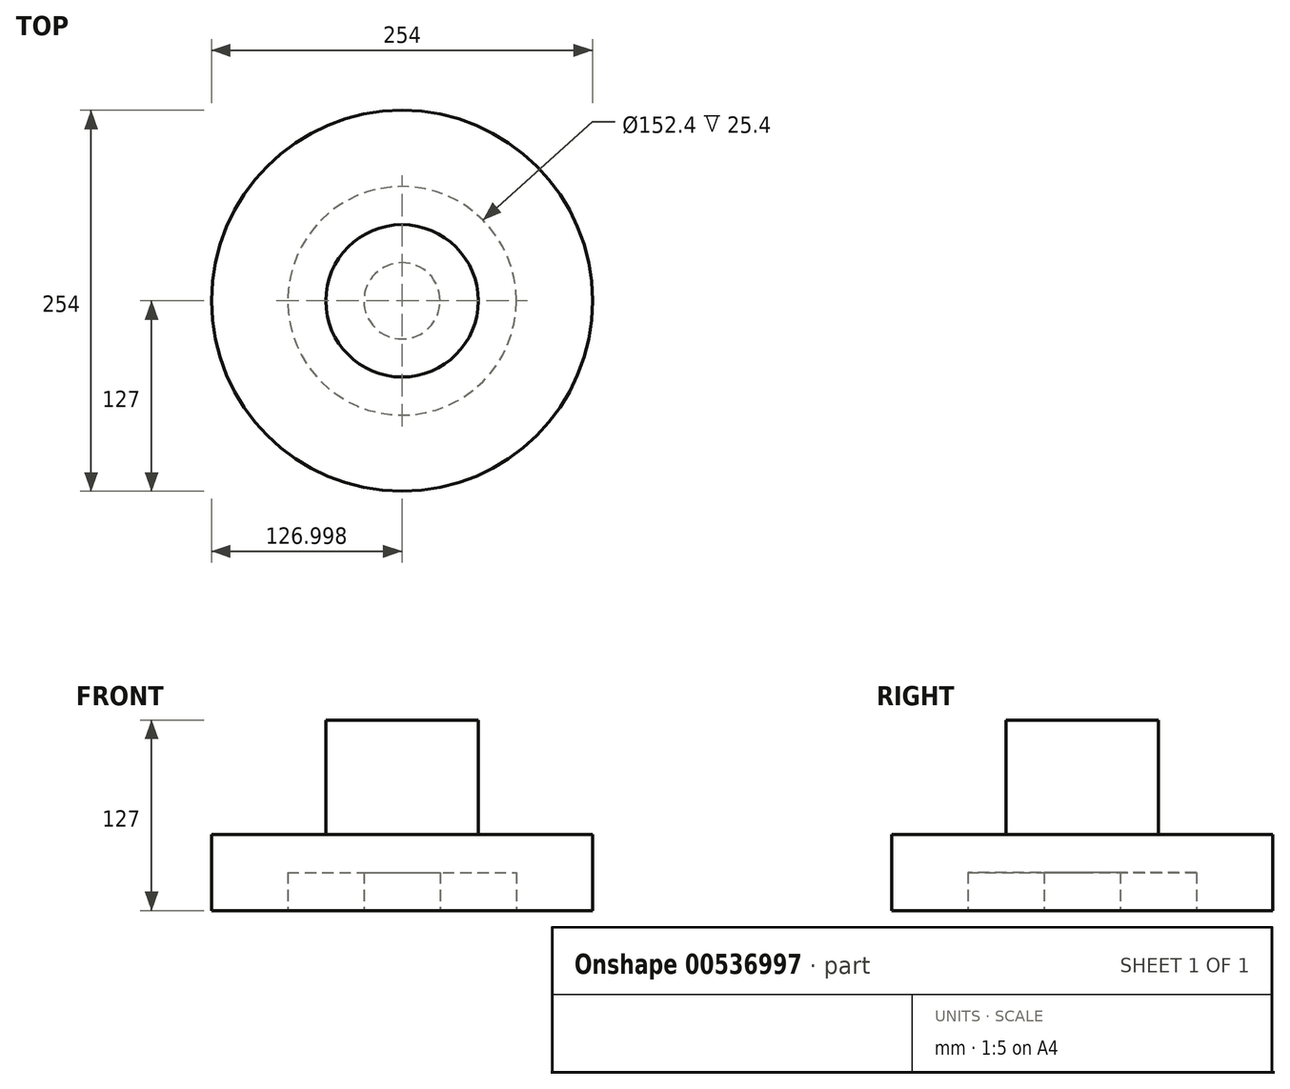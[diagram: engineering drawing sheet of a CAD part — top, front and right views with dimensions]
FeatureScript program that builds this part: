
annotation { "Feature Type Name" : "Feature", "Feature Type Description" : "" }
export const myFeature = defineFeature(function(context is Context, id is Id, definition is map)
    precondition{}
    {
        {
            var Q0;
            Q0=qCreatedBy(makeId("Front.planeOp"),FACE);
            var sketch = newSketch(context, id + "F0", { "sketchPlane" : qUnion([Q0])});
            skLineSegment(sketch, "E0", {"start": v(-71.72, 13.68) * mm, "end": v(-71.72, -37.12) * mm});
            skLineSegment(sketch, "E1", {"start": v(-71.72, -37.12) * mm, "end": v(-20.92, -37.12) * mm});
            skLineSegment(sketch, "E2", {"start": v(-20.92, -37.12) * mm, "end": v(-20.92, -11.72) * mm});
            skLineSegment(sketch, "E3", {"start": v(-20.92, -11.72) * mm, "end": v(29.88, -11.72) * mm});
            skLineSegment(sketch, "E4", {"start": v(29.88, -11.72) * mm, "end": v(29.88, -37.12) * mm});
            skLineSegment(sketch, "E5", {"start": v(29.88, -37.12) * mm, "end": v(55.28, -37.12) * mm});
            skLineSegment(sketch, "E6", {"start": v(55.28, -37.12) * mm, "end": v(55.28, 89.88) * mm});
            skLineSegment(sketch, "E7", {"start": v(55.28, 89.88) * mm, "end": v(4.48, 89.88) * mm});
            skLineSegment(sketch, "E8", {"start": v(4.48, 89.88) * mm, "end": v(4.48, 13.68) * mm});
            skLineSegment(sketch, "E9", {"start": v(4.48, 13.68) * mm, "end": v(-71.72, 13.68) * mm});
            skSolve(sketch);
        }
        {
            var Q0;
            Q0=makeQuery(id+"F0.imprint","IMPRINT",FACE,{"disambiguationData":[TD([[makeQuery(id+"F0.imprint","IMPRINT",EDGE,{"derivedFrom":sQuery(id+"F0.wireOp",EDGE,"E0")}),1.0]])]});
            var Q1;
            Q1=sQuery(id+"F0.wireOp",EDGE,"E6");
            revolve(context, id + "F1", {"entities" : qUnion([Q0]), "axis" : qUnion([Q1]), "revolveType" : RevolveType.FULL});
        }
    });
